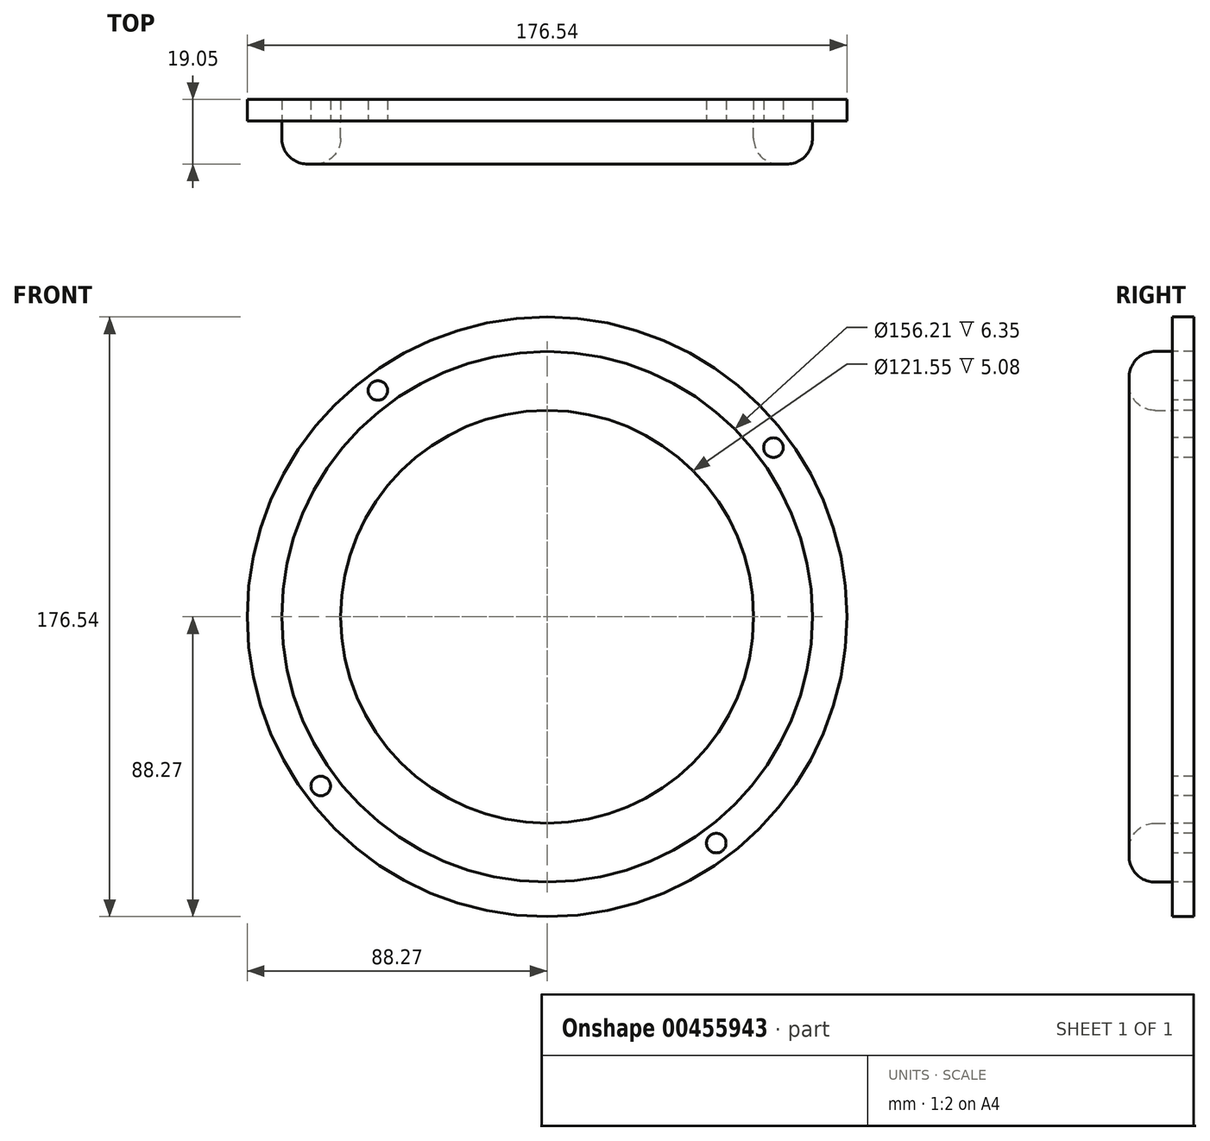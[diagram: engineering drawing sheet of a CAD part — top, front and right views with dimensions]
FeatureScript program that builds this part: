
annotation { "Feature Type Name" : "Feature", "Feature Type Description" : "" }
export const myFeature = defineFeature(function(context is Context, id is Id, definition is map)
    precondition{}
    {
        {
            var Q0;
            Q0=qCreatedBy(makeId("Front.planeOp"),FACE);
            var sketch = newSketch(context, id + "F0", { "sketchPlane" : qUnion([Q0])});
            skCircle(sketch, "E0", {"center": v(0, 0) * mm, "radius": 88.27 * mm});
            skCircle(sketch, "E1", {"center": v(0, 0) * mm, "radius": 78.1 * mm});
            skCircle(sketch, "E2", {"center": v(-49.8, 66.62) * mm, "radius": 2.88 * mm});
            skCircle(sketch, "E3.1.0", {"center": v(-66.62, -49.8) * mm, "radius": 2.88 * mm});
            skCircle(sketch, "E3.2.0", {"center": v(49.8, -66.62) * mm, "radius": 2.88 * mm});
            skCircle(sketch, "E3.3.0", {"center": v(66.62, 49.8) * mm, "radius": 2.88 * mm});
            skCircle(sketch, "E4", {"center": v(0, 0) * mm, "radius": 60.77 * mm});
            skSolve(sketch);
        }
        {
            var Q0;
            Q0=makeQuery(id+"F0.imprint","IMPRINT",FACE,{"disambiguationData":[TD([[makeQuery(id+"F0.imprint","IMPRINT",EDGE,{"derivedFrom":sQuery(id+"F0.wireOp",EDGE,"E1")}),1.0]])]});
            extrude(context, id + "F1", {"entities" : qUnion([Q0]), "depth" : 12.7 * mm, "offsetDistance" : 25.4 * mm});
        }
        {
            var Q0;
            Q0 = qSketchRegion(id + "F0", true);
            extrude(context, id + "F2", {"entities" : qUnion([Q0]), "depth" : -6.35 * mm, "offsetDistance" : 25.4 * mm});
        }
        {
            var Q0;
            Q0=makeQuery(id+"F1.opExtrude","CAP_EDGE",EDGE,{"disambiguationData":[OSD([sQuery(id+"F0.wireOp",EDGE,"E1")])],"isStart":false});
            var Q1;
            Q1=makeQuery(id+"F1.opExtrude","CAP_EDGE",EDGE,{"disambiguationData":[OSD([sQuery(id+"F0.wireOp",EDGE,"E4")])],"isStart":false});
            fillet(context, id + "F3", {"entities" : qUnion([Q0, Q1]), "tangentPropagation" : true, "radius" : 7.62 * mm, "defaultsChanged" : true, "vertexSettings" : [], "allowEdgeOverflow" : false});
        }
        {
            var Q0;
            Q0=makeQuery(id+"F0.imprint","IMPRINT",FACE,{"disambiguationData":[TD([[makeQuery(id+"F0.imprint","IMPRINT",EDGE,{"derivedFrom":sQuery(id+"F0.wireOp",EDGE,"E4")}),1.0]])]});
            extrude(context, id + "F4", {"entities" : qUnion([Q0]), "depth" : -6.35 * mm, "offsetDistance" : 25.4 * mm});
        }
    });
